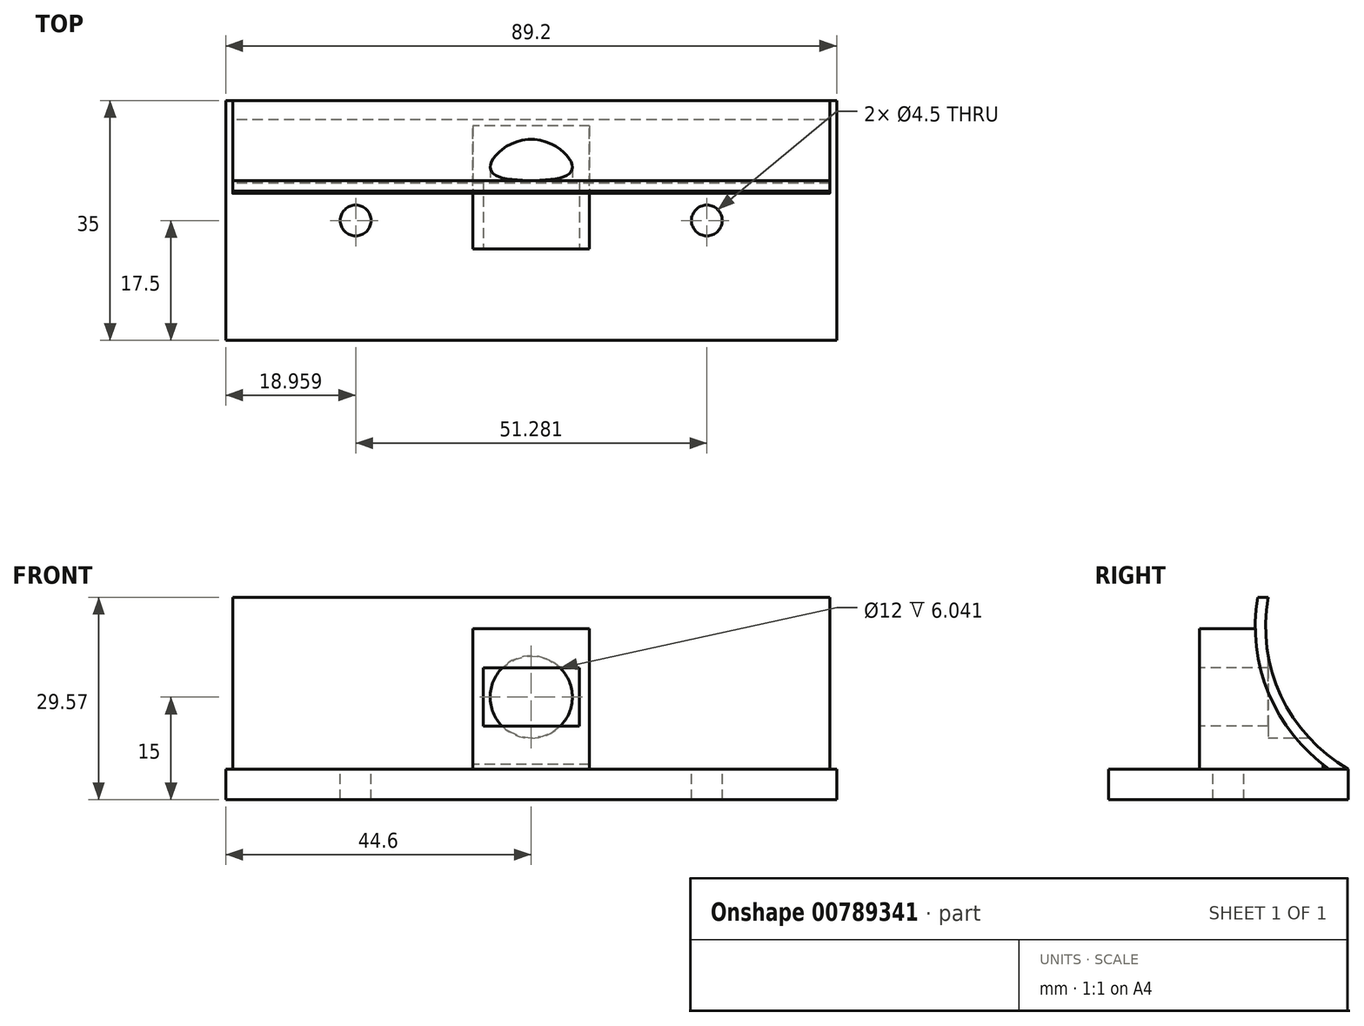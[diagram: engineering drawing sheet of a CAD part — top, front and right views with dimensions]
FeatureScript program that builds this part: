
annotation { "Feature Type Name" : "Feature", "Feature Type Description" : "" }
export const myFeature = defineFeature(function(context is Context, id is Id, definition is map)
    precondition{}
    {
        {
            var Q0;
            Q0=qCreatedBy(makeId("Top.planeOp"),FACE);
            var sketch = newSketch(context, id + "F0", { "sketchPlane" : qUnion([Q0])});
            skLineSegment(sketch, "E0.bottom", {"start": v(44.6, -17.5) * mm, "end": v(-44.6, -17.5) * mm});
            skLineSegment(sketch, "E0.top", {"start": v(44.6, 17.5) * mm, "end": v(-44.6, 17.5) * mm});
            skLineSegment(sketch, "E0.left", {"start": v(44.6, -17.5) * mm, "end": v(44.6, 17.5) * mm});
            skLineSegment(sketch, "E0.right", {"start": v(-44.6, -17.5) * mm, "end": v(-44.6, 17.5) * mm});
            skPoint(sketch, "E0.middle", {"position": v(0, 0) * mm});
            skLineSegment(sketch, "E1.bottom", {"start": v(8.5, -4.18) * mm, "end": v(-8.5, -4.18) * mm});
            skLineSegment(sketch, "E1.top", {"start": v(8.5, 13.82) * mm, "end": v(-8.5, 13.82) * mm});
            skLineSegment(sketch, "E1.left", {"start": v(8.5, -4.18) * mm, "end": v(8.5, 13.82) * mm});
            skLineSegment(sketch, "E1.right", {"start": v(-8.5, -4.18) * mm, "end": v(-8.5, 13.82) * mm});
            skPoint(sketch, "E1.middle", {"position": v(0, 4.82) * mm});
            skSolve(sketch);
        }
        {
            var Q0;
            Q0=makeQuery(id+"F0.imprint","IMPRINT",FACE,{"disambiguationData":[TD([[makeQuery(id+"F0.imprint","IMPRINT",EDGE,{"derivedFrom":sQuery(id+"F0.wireOp",EDGE,"E1.bottom")}),-1.0]])]});
            extrude(context, id + "F1", {"entities" : qUnion([Q0]), "depth" : 25 * mm, "offsetDistance" : 25 * mm});
        }
        {
            var Q0;
            Q0=makeQuery(id+"F0.imprint","IMPRINT",FACE,{"disambiguationData":[TD([[makeQuery(id+"F0.imprint","IMPRINT",EDGE,{"derivedFrom":sQuery(id+"F0.wireOp",EDGE,"E0.bottom")}),-1.0]])]});
            extrude(context, id + "F2", {"entities" : qUnion([Q0]), "operationType" : NewBodyOperationType.ADD, "depth" : 4.5 * mm, "offsetDistance" : 25 * mm});
        }
        {
            var Q0;
            Q0=makeQuery(id+"F2.opExtrude","CAP_FACE",FACE,{"disambiguationData":[OSD([sQuery(id+"F0.wireOp",EDGE,"E0.bottom"),sQuery(id+"F0.wireOp",EDGE,"E0.top"),sQuery(id+"F0.wireOp",EDGE,"E0.left"),sQuery(id+"F0.wireOp",EDGE,"E0.right"),sQuery(id+"F0.wireOp",EDGE,"E1.bottom"),sQuery(id+"F0.wireOp",EDGE,"E1.top"),sQuery(id+"F0.wireOp",EDGE,"E1.left"),sQuery(id+"F0.wireOp",EDGE,"E1.right")])],"isStart":false});
            var sketch = newSketch(context, id + "F3", { "sketchPlane" : qUnion([Q0])});
            skPoint(sketch, "E2", {"position": v(-25.64, 0) * mm});
            skPoint(sketch, "E3.MirrorP", {"position": v(25.64, 0) * mm});
            skSolve(sketch);
        }
        {
            var Q0;
            Q0=sQuery(id+"F3.wireOp",VERTEX,"E2");
            var Q1;
            Q1=sQuery(id+"F3.wireOp",VERTEX,"E3.MirrorP");
            var Q2;
            Q2=makeQuery(id+"F1.opExtrude","SWEPT_BODY",BODY,{"disambiguationData":[OSD([sQuery(id+"F0.wireOp",EDGE,"E1.bottom"),sQuery(id+"F0.wireOp",EDGE,"E1.top"),sQuery(id+"F0.wireOp",EDGE,"E1.left"),sQuery(id+"F0.wireOp",EDGE,"E1.right")])]});
            hole(context, id + "F4", {"style" : HoleStyle.SIMPLE, "endStyle" : HoleEndStyle.THROUGH, "holeDiameter" : 4.5 * mm, "majorDiameter" : 5 * mm, "isTappedThrough" : true, "tappedDepth" : 12 * mm, "tapClearance" : 3, "locations" : qUnion([Q0, Q1]), "scope" : qUnion([Q2])});
        }
        {
            var Q0;
            Q0=qCreatedBy(makeId("Right.planeOp"),FACE);
            var sketch = newSketch(context, id + "F5", { "sketchPlane" : qUnion([Q0])});
            skArc(sketch, "E4", {"start": v(5.82, 29.57) * mm, "mid": v(7.7, 15.19) * mm, "end": v(17.5, 4.5) * mm});
            skArc(sketch, "E5.0", {"start": v(4.3, 29.57) * mm, "mid": v(5.9, 15.54) * mm, "end": v(14.72, 4.5) * mm});
            skLineSegment(sketch, "E6", {"start": v(5.82, 29.57) * mm, "end": v(4.3, 29.57) * mm});
            skLineSegment(sketch, "E7", {"start": v(17.5, 4.5) * mm, "end": v(14.72, 4.5) * mm});
            skSolve(sketch);
        }
        {
            var Q0;
            Q0 = qSketchRegion(id + "F5", true);
            extrude(context, id + "F6", {"entities" : qUnion([Q0]), "operationType" : NewBodyOperationType.ADD, "endBound" : BoundingType.SYMMETRIC, "depth" : (89.2 - 2) * mm, "offsetDistance" : 25 * mm});
        }
        {
            var Q0;
            Q0=makeQuery(id+"F1.opExtrude","SWEPT_FACE",FACE,{"disambiguationData":[OSD([sQuery(id+"F0.wireOp",EDGE,"E1.bottom")])]});
            var sketch = newSketch(context, id + "F7", { "sketchPlane" : qUnion([Q0])});
            skLineSegment(sketch, "E8.bottom", {"start": v(7, 10.75) * mm, "end": v(-7, 10.75) * mm});
            skLineSegment(sketch, "E8.top", {"start": v(7, 19.25) * mm, "end": v(-7, 19.25) * mm});
            skLineSegment(sketch, "E8.left", {"start": v(7, 10.75) * mm, "end": v(7, 19.25) * mm});
            skLineSegment(sketch, "E8.right", {"start": v(-7, 10.75) * mm, "end": v(-7, 19.25) * mm});
            skPoint(sketch, "E8.middle", {"position": v(0, 15) * mm});
            skSolve(sketch);
        }
        {
            var Q0;
            Q0=makeQuery(id+"F7.imprint","IMPRINT",FACE,{"disambiguationData":[TD([[makeQuery(id+"F7.imprint","IMPRINT",EDGE,{"derivedFrom":sQuery(id+"F7.wireOp",EDGE,"E8.bottom")}),-1.0]])]});
            extrude(context, id + "F8", {"entities" : qUnion([Q0]), "operationType" : NewBodyOperationType.REMOVE, "oppositeDirection" : true, "depth" : 10 * mm, "offsetDistance" : 25 * mm});
        }
        {
            var Q0;
            Q0=makeQuery(id+"F8.boolean.opBoolean","COPY",FACE,{"derivedFrom":makeQuery(id+"F8.opExtrude","CAP_FACE",FACE,{"disambiguationData":[OSD([sQuery(id+"F7.wireOp",EDGE,"E8.bottom"),sQuery(id+"F7.wireOp",EDGE,"E8.top"),sQuery(id+"F7.wireOp",EDGE,"E8.left"),sQuery(id+"F7.wireOp",EDGE,"E8.right")])],"isStart":false})});
            var sketch = newSketch(context, id + "F9", { "sketchPlane" : qUnion([Q0])});
            skLineSegment(sketch, "E9", {"start": v(-7, 19.25) * mm, "end": v(7, 10.75) * mm, "construction": true});
            skPoint(sketch, "E10", {"position": v(0, 15) * mm});
            skCircle(sketch, "E11", {"center": v(0, 15) * mm, "radius": 6 * mm});
            skSolve(sketch);
        }
        {
            var Q0;
            {var subQ0=sQuery(id+"F9.wireOp",EDGE,"E11");var subQ1=makeQuery(id+"F8.boolean.opBoolean","COPY",EDGE,{"derivedFrom":makeQuery(id+"F8.opExtrude","CAP_EDGE",EDGE,{"disambiguationData":[OSD([sQuery(id+"F7.wireOp",EDGE,"E8.top")])],"isStart":false})});var subQ2=makeQuery(id+"F9.imprint","INTERSECT",VERTEX,{"disambiguationData":[OD(0.0)],"derivedFrom":[subQ1,subQ0]});Q0=makeQuery(id+"F9.imprint","IMPRINT",FACE,{"disambiguationData":[TD([[makeQuery(id+"F9.imprint","IMPRINT",EDGE,{"disambiguationData":[TD([[subQ2,1.0]])],"derivedFrom":subQ0}),1.0]])]});}
            var Q1;
            {var subQ0=sQuery(id+"F9.wireOp",EDGE,"E11");var subQ1=makeQuery(id+"F8.boolean.opBoolean","COPY",EDGE,{"derivedFrom":makeQuery(id+"F8.opExtrude","CAP_EDGE",EDGE,{"disambiguationData":[OSD([sQuery(id+"F7.wireOp",EDGE,"E8.bottom")])],"isStart":false})});var subQ2=makeQuery(id+"F9.imprint","INTERSECT",VERTEX,{"disambiguationData":[OD(0.0)],"derivedFrom":[subQ1,subQ0]});Q1=makeQuery(id+"F9.imprint","IMPRINT",FACE,{"disambiguationData":[TD([[makeQuery(id+"F9.imprint","IMPRINT",EDGE,{"disambiguationData":[TD([[subQ2,-1.0]])],"derivedFrom":subQ0}),1.0]])]});}
            var Q2;
            {var subQ0=sQuery(id+"F9.wireOp",EDGE,"E11");var subQ1=makeQuery(id+"F8.boolean.opBoolean","COPY",EDGE,{"derivedFrom":makeQuery(id+"F8.opExtrude","CAP_EDGE",EDGE,{"disambiguationData":[OSD([sQuery(id+"F7.wireOp",EDGE,"E8.top")])],"isStart":false})});var subQ2=makeQuery(id+"F9.imprint","INTERSECT",VERTEX,{"disambiguationData":[OD(0.0)],"derivedFrom":[subQ1,subQ0]});Q2=makeQuery(id+"F9.imprint","IMPRINT",FACE,{"disambiguationData":[TD([[makeQuery(id+"F9.imprint","IMPRINT",EDGE,{"disambiguationData":[TD([[subQ2,-1.0]])],"derivedFrom":subQ0}),1.0]])]});}
            extrude(context, id + "F10", {"entities" : qUnion([Q0, Q1, Q2]), "operationType" : NewBodyOperationType.REMOVE, "endBound" : BoundingType.THROUGH_ALL, "oppositeDirection" : true, "depth" : 25 * mm, "offsetDistance" : 25 * mm});
        }
        {
            var Q0;
            Q0=qCreatedBy(makeId("Right.planeOp"),FACE);
            var sketch = newSketch(context, id + "F11", { "sketchPlane" : qUnion([Q0])});
            skArc(sketch, "E12.0", {"start": v(5.82, 29.57) * mm, "mid": v(7.7, 15.19) * mm, "end": v(17.5, 4.5) * mm});
            skLineSegment(sketch, "E13", {"start": v(5.82, 29.57) * mm, "end": v(17.5, 29.57) * mm});
            skLineSegment(sketch, "E14", {"start": v(17.5, 29.57) * mm, "end": v(17.5, 4.5) * mm});
            skSolve(sketch);
        }
        {
            var Q0;
            Q0 = qSketchRegion(id + "F11", true);
            extrude(context, id + "F12", {"entities" : qUnion([Q0]), "operationType" : NewBodyOperationType.REMOVE, "endBound" : BoundingType.SYMMETRIC, "oppositeDirection" : true, "depth" : 89.2 * mm, "offsetDistance" : 25 * mm});
        }
    });
